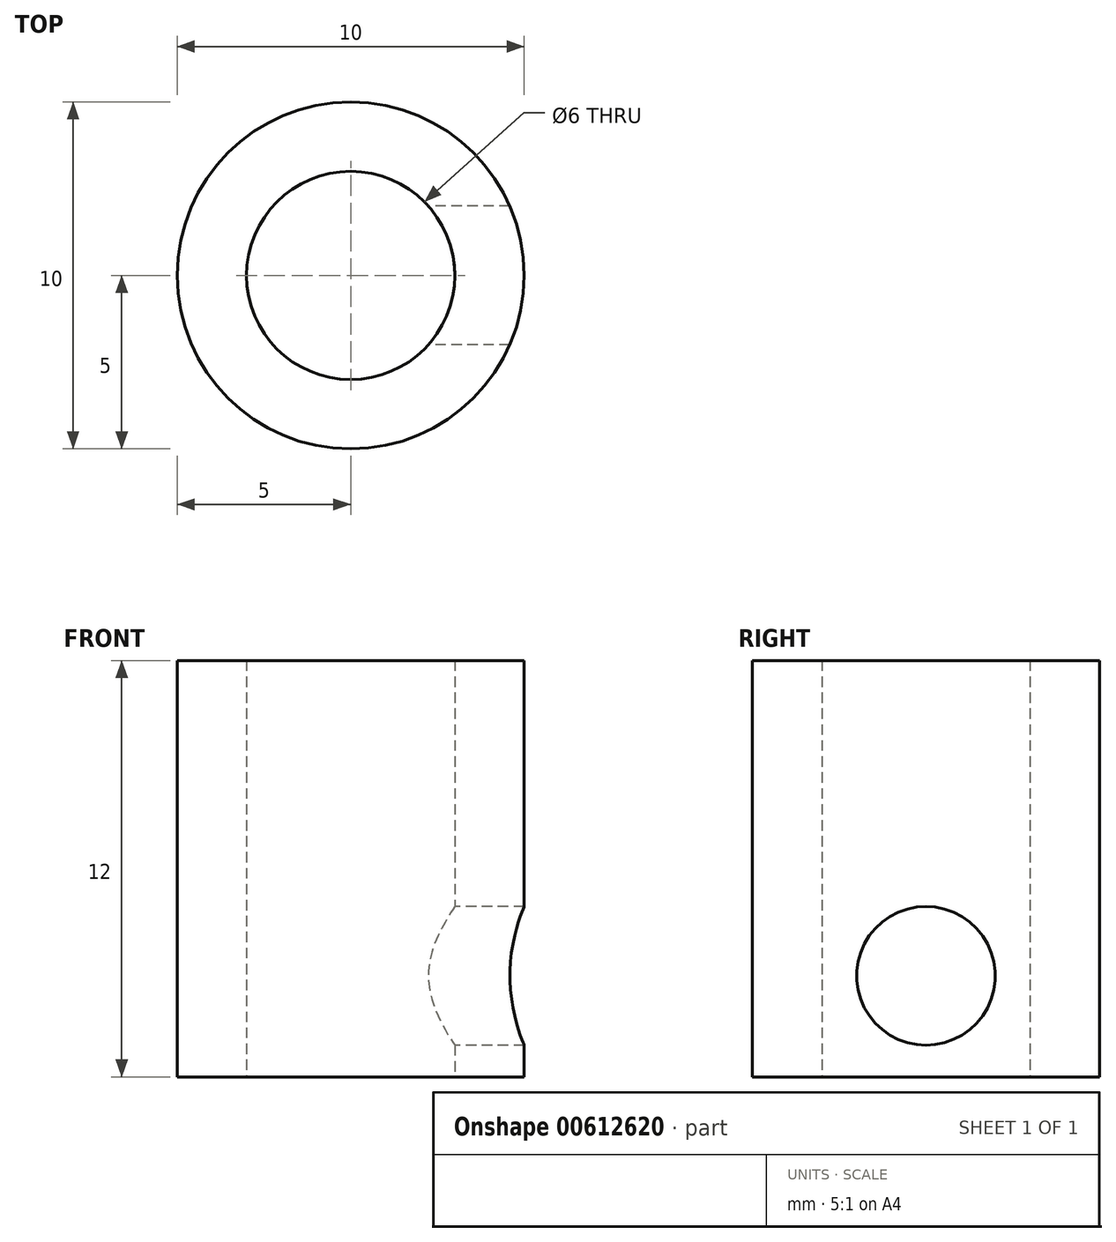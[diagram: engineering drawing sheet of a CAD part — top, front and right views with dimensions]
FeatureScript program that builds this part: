
annotation { "Feature Type Name" : "Feature", "Feature Type Description" : "" }
export const myFeature = defineFeature(function(context is Context, id is Id, definition is map)
    precondition{}
    {
        {
            var Q0;
            Q0=qCreatedBy(makeId("Top.planeOp"),FACE);
            var sketch = newSketch(context, id + "F0", { "sketchPlane" : qUnion([Q0])});
            skCircle(sketch, "E0", {"center": v(0, 0) * mm, "radius": 3 * mm});
            skCircle(sketch, "E1", {"center": v(0, 0) * mm, "radius": 5 * mm});
            skSolve(sketch);
        }
        {
            var Q0;
            Q0=makeQuery(id+"F0.imprint","IMPRINT",FACE,{"disambiguationData":[TD([[makeQuery(id+"F0.imprint","IMPRINT",EDGE,{"derivedFrom":sQuery(id+"F0.wireOp",EDGE,"E0")}),-1.0]])]});
            extrude(context, id + "F1", {"entities" : qUnion([Q0]), "depth" : 12 * mm, "offsetDistance" : 25 * mm});
        }
        {
            var Q0;
            Q0=qCreatedBy(makeId("Right.planeOp"),FACE);
            var sketch = newSketch(context, id + "F2", { "sketchPlane" : qUnion([Q0])});
            skPoint(sketch, "E2", {"position": v(0, 2.91) * mm});
            skSolve(sketch);
        }
        {
            var Q0;
            Q0=sQuery(id+"F2.wireOp",VERTEX,"E2");
            var Q1;
            Q1=makeQuery(id+"F1.opExtrude","SWEPT_BODY",BODY,{"disambiguationData":[OSD([sQuery(id+"F0.wireOp",EDGE,"E0"),sQuery(id+"F0.wireOp",EDGE,"E1")])]});
            hole(context, id + "F3", {"style" : HoleStyle.SIMPLE, "endStyle" : HoleEndStyle.THROUGH, "oppositeDirection" : true, "holeDiameter" : 4 * mm, "majorDiameter" : 5 * mm, "isTappedThrough" : true, "tappedDepth" : 12 * mm, "tapClearance" : 3, "locations" : qUnion([Q0]), "scope" : qUnion([Q1])});
        }
    });
